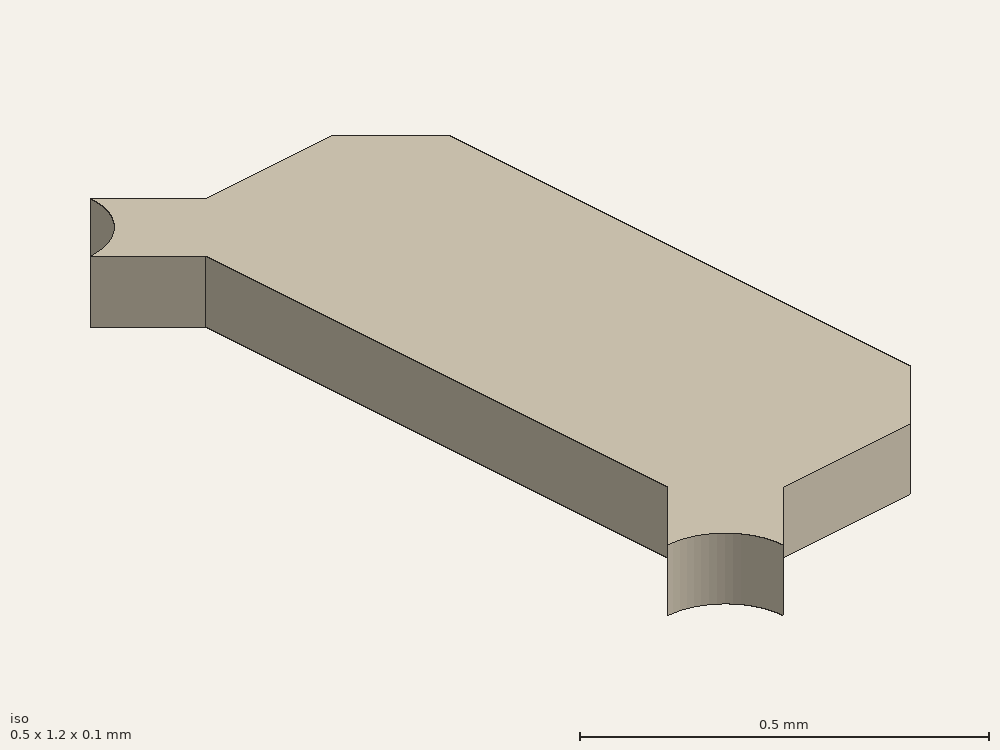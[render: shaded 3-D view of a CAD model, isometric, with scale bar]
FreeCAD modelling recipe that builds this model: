
FCSTD DOCUMENT  (FreeCAD 0.17R12607 (Git))
Label: FC-12M PAD 1bis
License: CreativeCommons Attribution-ShareAlike
LicenseURL: http://creativecommons.org/licenses/by-sa/4.0/
objects: Sketcher::SketchObject×1, PartDesign::Pad×1, PartDesign::Body×1
note: 4 computed .brp shape members not serialized (recipe doc carries the construction recipe); baked Part::Feature solids carry a one-line shape summary decoded from their .brp

FEATURE [Sketcher::SketchObject] Sketch
  MapMode = 5
  Support = -> [XY_Plane]
  sketch-geometry (15):
    g0: LineSegment StartX=-0.5 StartY=0.4 StartZ=0 EndX=-0.5 EndY=-0.4 EndZ=0
    g1: LineSegment StartX=-0.5 StartY=-0.4 StartZ=0 EndX=-0.6 EndY=-0.5 EndZ=0
    g2: LineSegment StartX=-0.6 StartY=-0.5 StartZ=0 EndX=-0.82 EndY=-0.5 EndZ=0
    g3: LineSegment StartX=-0.82 StartY=-0.5 StartZ=0 EndX=-0.92 EndY=-0.6 EndZ=0
    g4: LineSegment [constr] StartX=-0.92 StartY=-0.6 StartZ=0 EndX=-1.02 EndY=-0.5 EndZ=0
    g5: LineSegment StartX=-1.02 StartY=-0.5 StartZ=0 EndX=-0.92 EndY=-0.4 EndZ=0
    g6: LineSegment StartX=-0.92 StartY=-0.4 StartZ=0 EndX=-0.92 EndY=0.4 EndZ=0
    g7: LineSegment StartX=-0.92 StartY=0.4 StartZ=0 EndX=-1.02 EndY=0.5 EndZ=0
    g8: LineSegment [constr] StartX=-1.02 StartY=0.5 StartZ=0 EndX=-0.92 EndY=0.6 EndZ=0
    g9: LineSegment StartX=-0.92 StartY=0.6 StartZ=0 EndX=-0.82 EndY=0.5 EndZ=0
    g10: LineSegment StartX=-0.82 StartY=0.5 StartZ=0 EndX=-0.6 EndY=0.5 EndZ=0
    g11: LineSegment StartX=-0.6 StartY=0.5 StartZ=0 EndX=-0.5 EndY=0.4 EndZ=0
    g12: ArcOfCircle CenterX=-1.02 CenterY=0.6 CenterZ=0 NormalX=0 NormalY=0 NormalZ=1 AngleXU=0 Radius=0.1 StartAngle=4.71239 EndAngle=6.28319
    g13: LineSegment [constr] StartX=-1.02 StartY=0.5 StartZ=0 EndX=-0.82 EndY=0.5 EndZ=0
    g14: ArcOfCircle CenterX=-1.02 CenterY=-0.6 CenterZ=0 NormalX=0 NormalY=0 NormalZ=1 AngleXU=0 Radius=0.1 StartAngle=6.28319 EndAngle=7.85398
  constraints (42):
    c: Vertical(g0)
    c: Coincident(g0,g1)
    c: Coincident(g1,g2)
    c: Horizontal(g2)
    c: Coincident(g2,g3)
    c: Coincident(g3,g4)
    c: Coincident(g4,g5)
    c: Coincident(g5,g6)
    c: Vertical(g6)
    c: Coincident(g6,g7)
    c: Coincident(g7,g8)
    c: Coincident(g8,g9)
    c: Coincident(g9,g10)
    c: Horizontal(g10)
    c: Coincident(g10,g11)
    c: Coincident(g11,g0)
    c: Perpendicular(g7,g8)
    c: Perpendicular(g9,g8)
    c: Symmetric(g0,g0,g-1)
    c: Symmetric(g1,g10,g-1)
    c: Symmetric(g9,g2,g-1)
    c: Symmetric(g8,g3,g-1)
    c: Symmetric(g7,g4,g-1)
    c: Symmetric(g6,g5,g-1)
    c: DistanceX(g-2,g0) = -0.5
    c: Angle(g11,g0) = 2.35619
    c: DistanceX(g10,g10) = 0.22
    c: DistanceY(g0,g0) = 0.8
    c: Equal(g0,g6)
    c: Distance(g5,g0) = 0.42
    c: Angle(g7,g6) = 2.35619
    c: Equal(g8,g9)
    c: Distance(g4,g0) = 0.52
    c: Coincident(g12,g7)
    c: Coincident(g12,g8)
    c: Coincident(g13,g7)
    c: Coincident(g13,g9)
    c: Horizontal(g13)
    c: Tangent(g13,g12)
    c: Coincident(g14,g3)
    c: Coincident(g14,g4)
    c: Symmetric(g12,g14,g-1)
FEATURE [PartDesign::Pad] Pad
  Length = 0.1
  Length2 = 100
  Profile = -> Sketch
  Type = 0
FEATURE [PartDesign::Body] Body
  Group = -> [Sketch,Pad]
  Origin = -> Origin
  Tip = -> Pad
